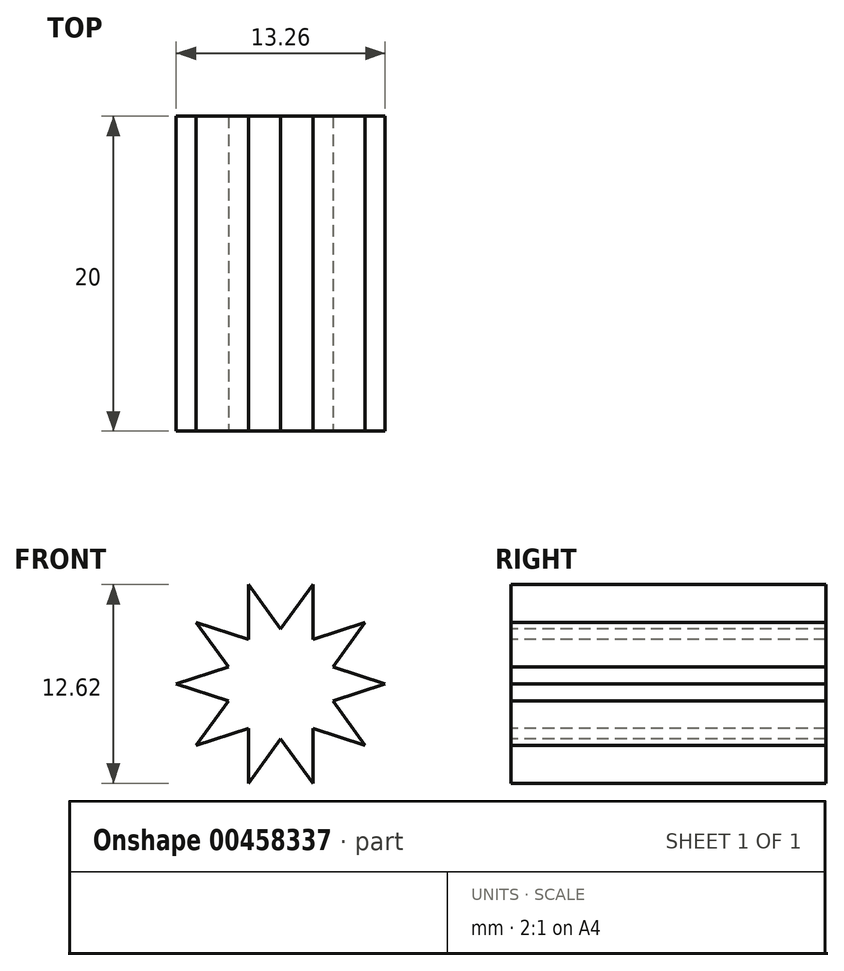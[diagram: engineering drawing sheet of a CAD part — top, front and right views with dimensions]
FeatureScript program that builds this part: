
annotation { "Feature Type Name" : "Feature", "Feature Type Description" : "" }
export const myFeature = defineFeature(function(context is Context, id is Id, definition is map)
    precondition{}
    {
        {
            var Q0;
            Q0=qCreatedBy(makeId("Front.planeOp"),FACE);
            var sketch = newSketch(context, id + "F0", { "sketchPlane" : qUnion([Q0])});
            skCircle(sketch, "E0", {"center": v(0, 0) * mm, "radius": 50 * mm});
            skArc(sketch, "E1", {"start": v(5.04, 60.29) * mm, "mid": v(0, 60.5) * mm, "end": v(-5.04, 60.29) * mm});
            skArc(sketch, "E2", {"start": v(-5.04, 60.29) * mm, "mid": v(-5.7, 54.98) * mm, "end": v(-6.05, 49.63) * mm});
            skArc(sketch, "E3.trimOffspring", {"start": v(6.05, 49.63) * mm, "mid": v(5.7, 54.98) * mm, "end": v(5.04, 60.29) * mm});
            skPoint(sketch, "E4.start.orphan", {"position": v(0, 46.5) * mm});
            skArc(sketch, "E5.1.0", {"start": v(-29.12, 53.03) * mm, "mid": v(-27.57, 47.9) * mm, "end": v(-25.71, 42.88) * mm});
            skArc(sketch, "E5.1.1", {"start": v(-19.92, 57.13) * mm, "mid": v(-24.6, 55.27) * mm, "end": v(-29.12, 53.03) * mm});
            skArc(sketch, "E5.1.2", {"start": v(-14.66, 47.8) * mm, "mid": v(-17.15, 52.54) * mm, "end": v(-19.92, 57.13) * mm});
            skArc(sketch, "E5.2.0", {"start": v(-48.17, 36.6) * mm, "mid": v(-44.67, 32.55) * mm, "end": v(-40.93, 28.72) * mm});
            skArc(sketch, "E5.2.1", {"start": v(-41.43, 44.09) * mm, "mid": v(-44.96, 40.48) * mm, "end": v(-48.17, 36.6) * mm});
            skArc(sketch, "E5.2.2", {"start": v(-32.84, 37.7) * mm, "mid": v(-37.04, 41.02) * mm, "end": v(-41.43, 44.09) * mm});
            skArc(sketch, "E5.3.0", {"start": v(-58.9, 13.84) * mm, "mid": v(-54.05, 11.57) * mm, "end": v(-49.07, 9.59) * mm});
            skArc(sketch, "E5.3.1", {"start": v(-55.78, 23.42) * mm, "mid": v(-57.54, 18.7) * mm, "end": v(-58.9, 13.84) * mm});
            skArc(sketch, "E5.3.2", {"start": v(-45.34, 21.09) * mm, "mid": v(-50.52, 22.4) * mm, "end": v(-55.78, 23.42) * mm});
            skArc(sketch, "E5.4.0", {"start": v(-59.43, -11.31) * mm, "mid": v(-54.08, -11.42) * mm, "end": v(-48.73, -11.2) * mm});
            skArc(sketch, "E5.4.1", {"start": v(-60.49, -1.3) * mm, "mid": v(-60.17, -6.32) * mm, "end": v(-59.43, -11.31) * mm});
            skArc(sketch, "E5.4.2", {"start": v(-50, 0.82) * mm, "mid": v(-55.27, -0.08) * mm, "end": v(-60.49, -1.3) * mm});
            skArc(sketch, "E5.5.0", {"start": v(-49.7, -34.5) * mm, "mid": v(-44.76, -32.42) * mm, "end": v(-39.96, -30.05) * mm});
            skArc(sketch, "E5.5.1", {"start": v(-54.73, -25.78) * mm, "mid": v(-52.4, -30.25) * mm, "end": v(-49.7, -34.5) * mm});
            skArc(sketch, "E5.5.2", {"start": v(-46, -19.58) * mm, "mid": v(-50.46, -22.55) * mm, "end": v(-54.73, -25.78) * mm});
            skArc(sketch, "E5.6.0", {"start": v(-31.36, -51.74) * mm, "mid": v(-27.7, -47.83) * mm, "end": v(-24.28, -43.7) * mm});
            skArc(sketch, "E5.6.1", {"start": v(-39.51, -45.81) * mm, "mid": v(-35.56, -48.95) * mm, "end": v(-31.36, -51.74) * mm});
            skArc(sketch, "E5.6.2", {"start": v(-34.06, -36.6) * mm, "mid": v(-36.93, -41.13) * mm, "end": v(-39.51, -45.81) * mm});
            skArc(sketch, "E5.7.0", {"start": v(-7.6, -60.02) * mm, "mid": v(-5.85, -54.96) * mm, "end": v(-4.4, -49.8) * mm});
            skArc(sketch, "E5.7.1", {"start": v(-17.46, -57.93) * mm, "mid": v(-12.58, -59.18) * mm, "end": v(-7.6, -60.02) * mm});
            skArc(sketch, "E5.7.2", {"start": v(-16.23, -47.3) * mm, "mid": v(-17, -52.6) * mm, "end": v(-17.46, -57.93) * mm});
            skArc(sketch, "E5.8.0", {"start": v(17.46, -57.93) * mm, "mid": v(17, -52.6) * mm, "end": v(16.23, -47.3) * mm});
            skArc(sketch, "E5.8.1", {"start": v(7.6, -60.02) * mm, "mid": v(12.58, -59.18) * mm, "end": v(17.46, -57.93) * mm});
            skArc(sketch, "E5.8.2", {"start": v(4.4, -49.8) * mm, "mid": v(5.85, -54.96) * mm, "end": v(7.6, -60.02) * mm});
            skArc(sketch, "E5.9.0", {"start": v(39.51, -45.81) * mm, "mid": v(36.93, -41.13) * mm, "end": v(34.06, -36.6) * mm});
            skArc(sketch, "E5.9.1", {"start": v(31.36, -51.74) * mm, "mid": v(35.56, -48.95) * mm, "end": v(39.51, -45.81) * mm});
            skArc(sketch, "E5.9.2", {"start": v(24.28, -43.7) * mm, "mid": v(27.7, -47.83) * mm, "end": v(31.36, -51.74) * mm});
            skArc(sketch, "E5.10.0", {"start": v(54.73, -25.78) * mm, "mid": v(50.46, -22.55) * mm, "end": v(46, -19.58) * mm});
            skArc(sketch, "E5.10.1", {"start": v(49.7, -34.5) * mm, "mid": v(52.4, -30.25) * mm, "end": v(54.73, -25.78) * mm});
            skArc(sketch, "E5.10.2", {"start": v(39.96, -30.05) * mm, "mid": v(44.76, -32.42) * mm, "end": v(49.7, -34.5) * mm});
            skArc(sketch, "E5.11.0", {"start": v(60.49, -1.3) * mm, "mid": v(55.27, -0.08) * mm, "end": v(50, 0.82) * mm});
            skArc(sketch, "E5.11.1", {"start": v(59.43, -11.31) * mm, "mid": v(60.17, -6.32) * mm, "end": v(60.49, -1.3) * mm});
            skArc(sketch, "E5.11.2", {"start": v(48.73, -11.2) * mm, "mid": v(54.08, -11.42) * mm, "end": v(59.43, -11.31) * mm});
            skArc(sketch, "E5.12.0", {"start": v(55.78, 23.42) * mm, "mid": v(50.52, 22.4) * mm, "end": v(45.34, 21.09) * mm});
            skArc(sketch, "E5.12.1", {"start": v(58.9, 13.84) * mm, "mid": v(57.54, 18.7) * mm, "end": v(55.78, 23.42) * mm});
            skArc(sketch, "E5.12.2", {"start": v(49.07, 9.59) * mm, "mid": v(54.05, 11.57) * mm, "end": v(58.9, 13.84) * mm});
            skArc(sketch, "E5.13.0", {"start": v(41.43, 44.09) * mm, "mid": v(37.04, 41.02) * mm, "end": v(32.84, 37.7) * mm});
            skArc(sketch, "E5.13.1", {"start": v(48.17, 36.6) * mm, "mid": v(44.96, 40.48) * mm, "end": v(41.43, 44.09) * mm});
            skArc(sketch, "E5.13.2", {"start": v(40.93, 28.72) * mm, "mid": v(44.67, 32.55) * mm, "end": v(48.17, 36.6) * mm});
            skArc(sketch, "E5.14.0", {"start": v(19.92, 57.13) * mm, "mid": v(17.15, 52.54) * mm, "end": v(14.66, 47.8) * mm});
            skArc(sketch, "E5.14.1", {"start": v(29.12, 53.03) * mm, "mid": v(24.6, 55.27) * mm, "end": v(19.92, 57.13) * mm});
            skArc(sketch, "E5.14.2", {"start": v(25.71, 42.88) * mm, "mid": v(27.57, 47.9) * mm, "end": v(29.12, 53.03) * mm});
            skSolve(sketch);
        }
        {
            var Q0;
            Q0=qCreatedBy(makeId("Front.planeOp"),FACE);
            var sketch = newSketch(context, id + "F1", { "sketchPlane" : qUnion([Q0])});
            skCircle(sketch, "E6", {"center": v(0, 0) * mm, "radius": 10.5 * mm});
            skLineSegment(sketch, "E7.bottom", {"start": v(-2.05, -12.45) * mm, "end": v(2.05, -12.45) * mm});
            skLineSegment(sketch, "E7.top", {"start": v(-2.05, 12.65) * mm, "end": v(2.05, 12.65) * mm});
            skLineSegment(sketch, "E7.left", {"start": v(-2.05, -12.45) * mm, "end": v(-2.05, 12.65) * mm});
            skLineSegment(sketch, "E7.right", {"start": v(2.05, -12.45) * mm, "end": v(2.05, 12.65) * mm});
            skLineSegment(sketch, "E8.1.0", {"start": v(8.98, -8.87) * mm, "end": v(-5.78, 11.44) * mm});
            skLineSegment(sketch, "E8.1.1", {"start": v(-9.1, 9.03) * mm, "end": v(-5.78, 11.44) * mm});
            skLineSegment(sketch, "E8.1.2", {"start": v(5.66, -11.28) * mm, "end": v(-9.1, 9.03) * mm});
            skLineSegment(sketch, "E8.2.0", {"start": v(12.47, -1.9) * mm, "end": v(-11.4, 5.86) * mm});
            skLineSegment(sketch, "E8.2.1", {"start": v(-12.66, 1.96) * mm, "end": v(-11.4, 5.86) * mm});
            skLineSegment(sketch, "E8.2.2", {"start": v(11.2, -5.8) * mm, "end": v(-12.66, 1.96) * mm});
            skLineSegment(sketch, "E8.3.0", {"start": v(11.2, 5.8) * mm, "end": v(-12.66, -1.96) * mm});
            skLineSegment(sketch, "E8.3.1", {"start": v(-11.4, -5.86) * mm, "end": v(-12.66, -1.96) * mm});
            skLineSegment(sketch, "E8.3.2", {"start": v(12.47, 1.9) * mm, "end": v(-11.4, -5.86) * mm});
            skLineSegment(sketch, "E8.4.0", {"start": v(5.66, 11.28) * mm, "end": v(-9.1, -9.03) * mm});
            skLineSegment(sketch, "E8.4.1", {"start": v(-5.78, -11.44) * mm, "end": v(-9.1, -9.03) * mm});
            skLineSegment(sketch, "E8.4.2", {"start": v(8.98, 8.87) * mm, "end": v(-5.78, -11.44) * mm});
            skLineSegment(sketch, "E8.5.0", {"start": v(-2.05, 12.45) * mm, "end": v(-2.05, -12.65) * mm});
            skLineSegment(sketch, "E8.5.1", {"start": v(2.05, -12.65) * mm, "end": v(-2.05, -12.65) * mm});
            skLineSegment(sketch, "E8.5.2", {"start": v(2.05, 12.45) * mm, "end": v(2.05, -12.65) * mm});
            skLineSegment(sketch, "E8.6.0", {"start": v(-8.98, 8.87) * mm, "end": v(5.78, -11.44) * mm});
            skLineSegment(sketch, "E8.6.1", {"start": v(9.1, -9.03) * mm, "end": v(5.78, -11.44) * mm});
            skLineSegment(sketch, "E8.6.2", {"start": v(-5.66, 11.28) * mm, "end": v(9.1, -9.03) * mm});
            skLineSegment(sketch, "E8.7.0", {"start": v(-12.47, 1.9) * mm, "end": v(11.4, -5.86) * mm});
            skLineSegment(sketch, "E8.7.1", {"start": v(12.66, -1.96) * mm, "end": v(11.4, -5.86) * mm});
            skLineSegment(sketch, "E8.7.2", {"start": v(-11.2, 5.8) * mm, "end": v(12.66, -1.96) * mm});
            skLineSegment(sketch, "E8.8.0", {"start": v(-11.2, -5.8) * mm, "end": v(12.66, 1.96) * mm});
            skLineSegment(sketch, "E8.8.1", {"start": v(11.4, 5.86) * mm, "end": v(12.66, 1.96) * mm});
            skLineSegment(sketch, "E8.8.2", {"start": v(-12.47, -1.9) * mm, "end": v(11.4, 5.86) * mm});
            skLineSegment(sketch, "E8.9.0", {"start": v(-5.66, -11.28) * mm, "end": v(9.1, 9.03) * mm});
            skLineSegment(sketch, "E8.9.1", {"start": v(5.78, 11.44) * mm, "end": v(9.1, 9.03) * mm});
            skLineSegment(sketch, "E8.9.2", {"start": v(-8.98, -8.87) * mm, "end": v(5.78, 11.44) * mm});
            skSolve(sketch);
        }
        {
            var Q0;
            Q0 = qSketchRegion(id + "F0", true);
            extrude(context, id + "F2", {"entities" : qUnion([Q0]), "depth" : 20 * mm, "symmetric" : true});
        }
        {
            var Q0;
            Q0 = qSketchRegion(id + "F1", true);
            extrude(context, id + "F3", {"entities" : qUnion([Q0]), "operationType" : NewBodyOperationType.REMOVE, "oppositeDirection" : true, "depth" : 20 * mm, "symmetric" : true});
        }
        {
            var Q0;
            {var subQ13=sQuery(id+"F1.wireOp",EDGE,"E8.6.2");var subQ14=sQuery(id+"F1.wireOp",EDGE,"E8.5.0");var subQ15=makeQuery(id+"F1.imprint","INTERSECT",VERTEX,{"derivedFrom":[subQ14,subQ13]});Q0=makeQuery(id+"F3.boolean.opBoolean","SPLIT",FACE,{"disambiguationData":[TD([makeQuery(id+"F3.opExtrude","SWEPT_FACE",FACE,{"disambiguationData":[OSD([subQ14]),TDD([makeQuery(id+"F1.imprint","IMPRINT",EDGE,{"disambiguationData":[TD([[subQ15,-1.0]])],"derivedFrom":subQ14})])]})])],"derivedFrom":makeQuery(id+"F2.opExtrude","CAP_FACE",FACE,{"disambiguationData":[OSD([sQuery(id+"F0.wireOp",EDGE,"E0"),sQuery(id+"F0.wireOp",EDGE,"E1"),sQuery(id+"F0.wireOp",EDGE,"E2"),sQuery(id+"F0.wireOp",EDGE,"E3.trimOffspring"),sQuery(id+"F0.wireOp",EDGE,"E5.1.0"),sQuery(id+"F0.wireOp",EDGE,"E5.1.1"),sQuery(id+"F0.wireOp",EDGE,"E5.1.2"),sQuery(id+"F0.wireOp",EDGE,"E5.2.0"),sQuery(id+"F0.wireOp",EDGE,"E5.2.1"),sQuery(id+"F0.wireOp",EDGE,"E5.2.2"),sQuery(id+"F0.wireOp",EDGE,"E5.3.0"),sQuery(id+"F0.wireOp",EDGE,"E5.3.1"),sQuery(id+"F0.wireOp",EDGE,"E5.3.2"),sQuery(id+"F0.wireOp",EDGE,"E5.4.0"),sQuery(id+"F0.wireOp",EDGE,"E5.4.1"),sQuery(id+"F0.wireOp",EDGE,"E5.4.2"),sQuery(id+"F0.wireOp",EDGE,"E5.5.0"),sQuery(id+"F0.wireOp",EDGE,"E5.5.1"),sQuery(id+"F0.wireOp",EDGE,"E5.5.2"),sQuery(id+"F0.wireOp",EDGE,"E5.6.0"),sQuery(id+"F0.wireOp",EDGE,"E5.6.1"),sQuery(id+"F0.wireOp",EDGE,"E5.6.2"),sQuery(id+"F0.wireOp",EDGE,"E5.7.0"),sQuery(id+"F0.wireOp",EDGE,"E5.7.1"),sQuery(id+"F0.wireOp",EDGE,"E5.7.2"),sQuery(id+"F0.wireOp",EDGE,"E5.8.0"),sQuery(id+"F0.wireOp",EDGE,"E5.8.1"),sQuery(id+"F0.wireOp",EDGE,"E5.8.2"),sQuery(id+"F0.wireOp",EDGE,"E5.9.0"),sQuery(id+"F0.wireOp",EDGE,"E5.9.1"),sQuery(id+"F0.wireOp",EDGE,"E5.9.2"),sQuery(id+"F0.wireOp",EDGE,"E5.10.0"),sQuery(id+"F0.wireOp",EDGE,"E5.10.1"),sQuery(id+"F0.wireOp",EDGE,"E5.10.2"),sQuery(id+"F0.wireOp",EDGE,"E5.11.0"),sQuery(id+"F0.wireOp",EDGE,"E5.11.1"),sQuery(id+"F0.wireOp",EDGE,"E5.11.2"),sQuery(id+"F0.wireOp",EDGE,"E5.12.0"),sQuery(id+"F0.wireOp",EDGE,"E5.12.1"),sQuery(id+"F0.wireOp",EDGE,"E5.12.2"),sQuery(id+"F0.wireOp",EDGE,"E5.13.0"),sQuery(id+"F0.wireOp",EDGE,"E5.13.1"),sQuery(id+"F0.wireOp",EDGE,"E5.13.2"),sQuery(id+"F0.wireOp",EDGE,"E5.14.0"),sQuery(id+"F0.wireOp",EDGE,"E5.14.1"),sQuery(id+"F0.wireOp",EDGE,"E5.14.2")])],"isStart":false})});}
            extrude(context, id + "F4", {"entities" : qUnion([Q0]), "operationType" : NewBodyOperationType.REMOVE, "oppositeDirection" : true, "depth" : 20 * mm});
        }
    });
